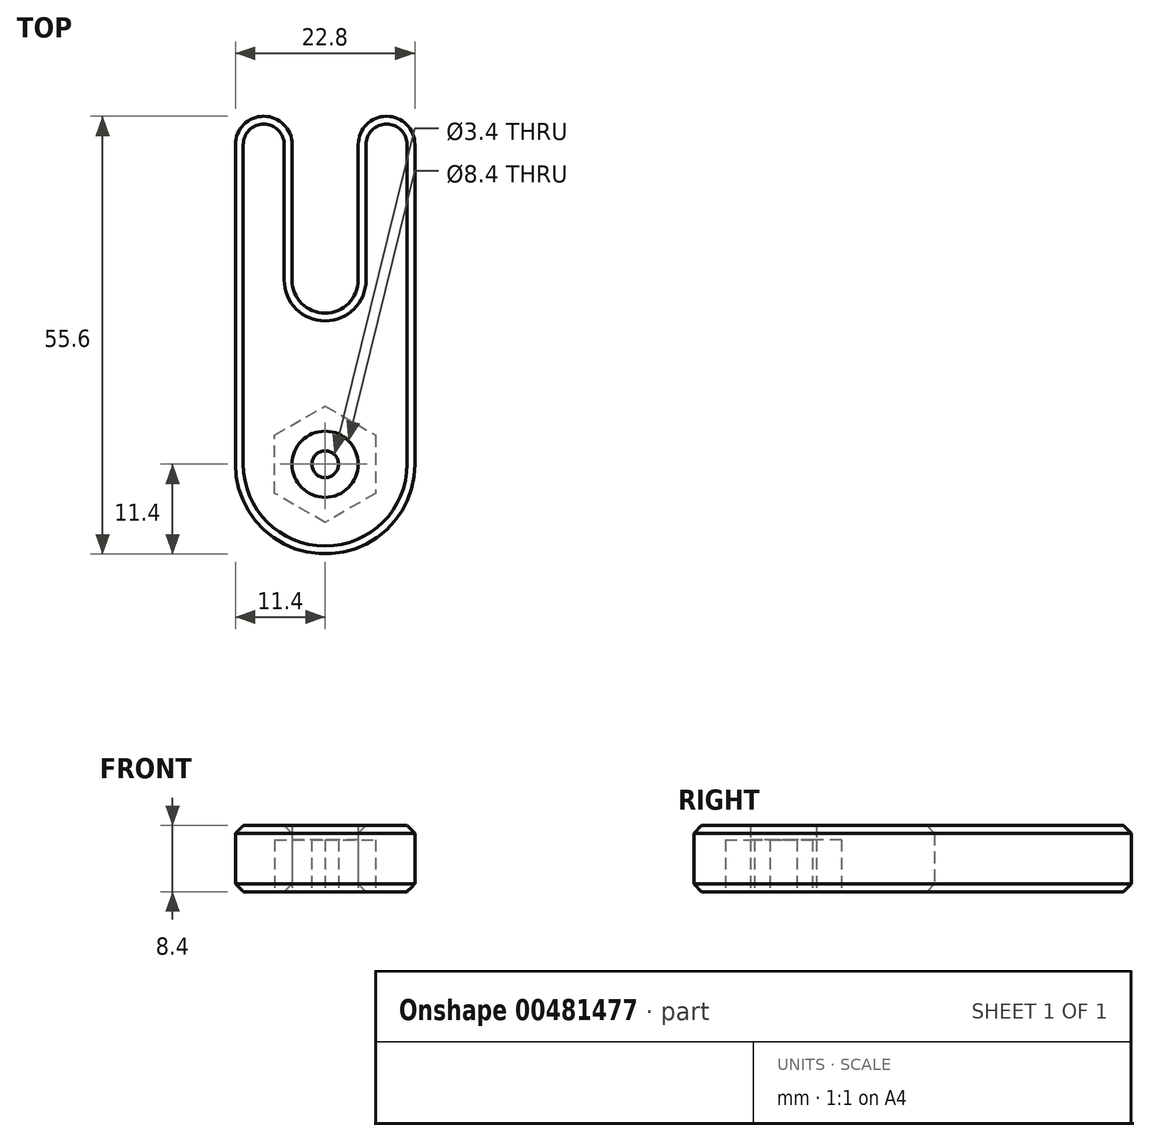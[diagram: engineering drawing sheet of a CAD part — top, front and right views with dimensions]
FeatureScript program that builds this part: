
annotation { "Feature Type Name" : "Feature", "Feature Type Description" : "" }
export const myFeature = defineFeature(function(context is Context, id is Id, definition is map)
    precondition{}
    {
        {
            var Q0;
            Q0=qCreatedBy(makeId("Top.planeOp"),FACE);
            var sketch = newSketch(context, id + "F0", { "sketchPlane" : qUnion([Q0])});
            skCircle(sketch, "E0", {"center": v(0, 0) * mm, "radius": 4.2 * mm});
            skCircle(sketch, "E1", {"center": v(0, -23.4) * mm, "radius": 4.2 * mm});
            skCircle(sketch, "E2.cCircle", {"center": v(0, -23.4) * mm, "radius": 6.4 * mm, "construction": true});
            skLineSegment(sketch, "E2.0", {"start": v(6.4, -19.7) * mm, "end": v(6.4, -27.1) * mm});
            skLineSegment(sketch, "E2.1", {"start": v(6.4, -27.1) * mm, "end": v(0, -30.8) * mm});
            skLineSegment(sketch, "E2.2", {"start": v(0, -30.8) * mm, "end": v(-6.4, -27.1) * mm});
            skLineSegment(sketch, "E2.3", {"start": v(-6.4, -27.1) * mm, "end": v(-6.4, -19.7) * mm});
            skLineSegment(sketch, "E2.4", {"start": v(-6.4, -19.7) * mm, "end": v(0, -16) * mm});
            skLineSegment(sketch, "E2.5", {"start": v(0, -16) * mm, "end": v(6.4, -19.7) * mm});
            skPoint(sketch, "E2.0.midPoint", {"position": v(6.4, -23.4) * mm});
            skLineSegment(sketch, "E3", {"start": v(-11.4, -23.4) * mm, "end": v(-11.4, 17.2) * mm});
            skLineSegment(sketch, "E4", {"start": v(-4.2, 0) * mm, "end": v(-4.2, 17.2) * mm});
            skLineSegment(sketch, "E5", {"start": v(4.2, 0) * mm, "end": v(4.2, 17.2) * mm});
            skLineSegment(sketch, "E6", {"start": v(11.4, 17.2) * mm, "end": v(11.4, -23.4) * mm});
            skArc(sketch, "E7", {"start": v(-11.4, -23.4) * mm, "mid": v(0, -34.8) * mm, "end": v(11.4, -23.4) * mm});
            skArc(sketch, "E8", {"start": v(-4.2, 17.2) * mm, "mid": v(-7.8, 20.8) * mm, "end": v(-11.4, 17.2) * mm});
            skArc(sketch, "E9", {"start": v(11.4, 17.2) * mm, "mid": v(7.8, 20.8) * mm, "end": v(4.2, 17.2) * mm});
            skLineSegment(sketch, "E10", {"start": v(-7.8, 20.8) * mm, "end": v(7.8, 20.8) * mm, "construction": true});
            skLineSegment(sketch, "E11", {"start": v(-11.4, -34.8) * mm, "end": v(11.4, -34.8) * mm, "construction": true});
            skSolve(sketch);
        }
        {
            var Q0;
            Q0=makeQuery(id+"F0.imprint","IMPRINT",FACE,{"disambiguationData":[TD([[makeQuery(id+"F0.imprint","IMPRINT",EDGE,{"derivedFrom":sQuery(id+"F0.wireOp",EDGE,"E2.0")}),1.0]])]});
            var Q1;
            Q1=makeQuery(id+"F0.imprint","IMPRINT",FACE,{"disambiguationData":[TD([[makeQuery(id+"F0.imprint","IMPRINT",EDGE,{"derivedFrom":sQuery(id+"F0.wireOp",EDGE,"E1")}),-1.0]])]});
            extrude(context, id + "F1", {"entities" : qUnion([Q0, Q1]), "depth" : (1.8 + 6.6) * mm});
        }
        {
            var Q0;
            Q0=makeQuery(id+"F0.imprint","IMPRINT",FACE,{"disambiguationData":[TD([[makeQuery(id+"F0.imprint","IMPRINT",EDGE,{"derivedFrom":sQuery(id+"F0.wireOp",EDGE,"E1")}),-1.0]])]});
            extrude(context, id + "F2", {"entities" : qUnion([Q0]), "operationType" : NewBodyOperationType.REMOVE, "depth" : 6.6 * mm});
        }
        {
            var Q0;
            Q0=makeQuery(id+"F0.imprint","IMPRINT",FACE,{"disambiguationData":[TD([[makeQuery(id+"F0.imprint","IMPRINT",EDGE,{"derivedFrom":sQuery(id+"F0.wireOp",EDGE,"E1")}),1.0]])]});
            extrude(context, id + "F3", {"entities" : qUnion([Q0]), "depth" : 6.6 * mm});
        }
        {
            var Q0;
            Q0=makeQuery(id+"F3.opExtrude","CAP_FACE",FACE,{"disambiguationData":[OSD([sQuery(id+"F0.wireOp",EDGE,"E1")])],"isStart":false});
            var Q1;
            Q1=makeQuery(id+"F3.opExtrude","CAP_FACE",FACE,{"disambiguationData":[OSD([sQuery(id+"F0.wireOp",EDGE,"E1")])],"isStart":true});
            shell(context, id + "F4", {"entities" : qUnion([Q0, Q1]), "thickness" : 2.5 * mm});
        }
        {
            var Q0;
            Q0=makeQuery(id+"F1.opExtrude","CAP_EDGE",EDGE,{"disambiguationData":[OSD([sQuery(id+"F0.wireOp",EDGE,"E6")])],"isStart":false});
            var Q1;
            Q1=makeQuery(id+"F1.opExtrude","CAP_EDGE",EDGE,{"disambiguationData":[OSD([sQuery(id+"F0.wireOp",EDGE,"E3")])],"isStart":true});
            chamfer(context, id + "F5", {"entities" : qUnion([Q0, Q1]), "width" : 1 * mm, "tangentPropagation" : true});
        }
    });
